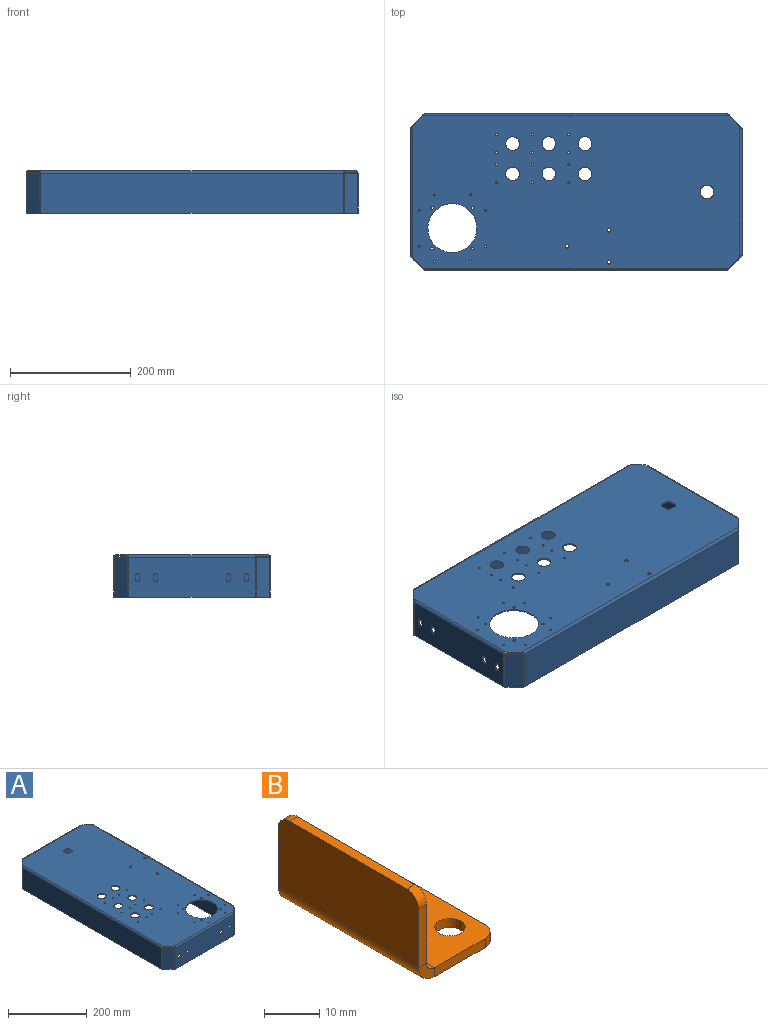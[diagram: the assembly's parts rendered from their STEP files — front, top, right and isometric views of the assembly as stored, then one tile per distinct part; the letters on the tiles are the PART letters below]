
ASSEMBLY  parts=2 mates=1
PART A: 140 faces, bbox 260x550x70 mm
  f0: plane 4.66x2mm, normal (0,-1,0), area 9.3mm2, adj f2,f3,f4,f119
  f1: plane 4.66x2mm, normal (0,1,0), area 9.3mm2, adj f3,f4,f6,f76
  f2: plane 16.83x16.83mm, normal (-0.71,-0.71,0), area 47.6mm2, adj f0,f3,f4,f127
  f3: plane 542x252mm, normal (0,0,1), area 127773.2mm2, adj f0,f1,f2,f5,f6,f7,f8,f9
  f4: plane 542x252mm, normal (0,0,-1), area 127773.2mm2, adj f0,f1,f2,f5,f6,f7,f8,f9
  f5: plane 16.83x16.83mm, normal (0.71,-0.71,0), area 47.6mm2, adj f3,f4,f15,f137
  f6: plane 16.83x16.83mm, normal (0.71,0.71,0), area 47.6mm2, adj f1,f3,f4,f136
  f7: plane 16.83x16.83mm, normal (-0.71,0.71,0), area 47.6mm2, adj f3,f4,f16,f128
  f8: cylinder r=11.25mm len=4.99mm, axis (0,0,1), area 14.4mm2, adj f3,f4,f9,f51
  f9: plane 10.11x2mm, normal (-1,0,0), area 20.2mm2, adj f3,f4,f8,f10
  f10: cylinder r=11.25mm len=4.99mm, axis (0,0,1), area 14.4mm2, adj f3,f4,f9,f11
  f11: plane 10.11x2mm, normal (0,-1,0), area 20.2mm2, adj f3,f4,f10,f12
  f12: cylinder r=11.25mm len=4.99mm, axis (0,0,1), area 14.4mm2, adj f3,f4,f11,f13
  f13: plane 10.11x2mm, normal (1,0,0), area 20.2mm2, adj f3,f4,f12,f14
  f14: cylinder r=11.25mm len=4.99mm, axis (0,0,1), area 14.4mm2, adj f3,f4,f13,f51
  f15: plane 4.66x2mm, normal (0,-1,0), area 9.3mm2, adj f3,f4,f5,f118
  f16: plane 4.66x2mm, normal (0,1,0), area 9.3mm2, adj f3,f4,f7,f75
  f17: cylinder r=11.25mm len=22.5mm, axis (0,0,1), area 141.4mm2, adj f3,f4
  f18: cylinder r=11.25mm len=22.5mm, axis (0,0,1), area 141.4mm2, adj f3,f4
  f19: cylinder r=11.25mm len=22.5mm, axis (0,0,1), area 141.4mm2, adj f3,f4
  f20: cylinder r=11.25mm len=22.5mm, axis (0,0,1), area 141.4mm2, adj f3,f4
  f21: cylinder r=11.25mm len=22.5mm, axis (0,0,1), area 141.4mm2, adj f3,f4
  f22: cylinder r=11.25mm len=22.5mm, axis (0,0,1), area 141.4mm2, adj f3,f4
  f23: cylinder r=1.75mm len=3.5mm, axis (0,0,1), area 22mm2, adj f3,f4
  f24: cylinder r=1.75mm len=3.5mm, axis (0,0,1), area 22mm2, adj f3,f4
  f25: cylinder r=1.75mm len=3.5mm, axis (0,0,1), area 22mm2, adj f3,f4
  f26: cylinder r=1.75mm len=3.5mm, axis (0,0,1), area 22mm2, adj f3,f4
  f27: cylinder r=1.75mm len=3.5mm, axis (0,0,1), area 22mm2, adj f3,f4
  f28: cylinder r=1.75mm len=3.5mm, axis (0,0,1), area 22mm2, adj f3,f4
  f29: cylinder r=1.75mm len=3.5mm, axis (0,0,1), area 22mm2, adj f3,f4
  f30: cylinder r=1.75mm len=3.5mm, axis (0,0,1), area 22mm2, adj f3,f4
  f31: cylinder r=1.75mm len=3.5mm, axis (0,0,1), area 22mm2, adj f3,f4
  f32: cylinder r=1.75mm len=3.5mm, axis (0,0,1), area 22mm2, adj f3,f4
  f33: cylinder r=1.75mm len=3.5mm, axis (0,0,1), area 22mm2, adj f3,f4
  f34: cylinder r=1.75mm len=3.5mm, axis (0,0,1), area 22mm2, adj f3,f4
  f35: cylinder r=3mm len=6mm, axis (0,0,1), area 37.7mm2, adj f3,f4
  f36: cylinder r=1.75mm len=3.5mm, axis (0,0,1), area 22mm2, adj f3,f4
  f37: cylinder r=1.75mm len=3.5mm, axis (0,0,1), area 22mm2, adj f3,f4
  f38: cylinder r=2.25mm len=4.5mm, axis (0,0,1), area 28.3mm2, adj f3,f4
  f39: cylinder r=2.25mm len=4.5mm, axis (0,0,1), area 28.3mm2, adj f3,f4
  f40: cylinder r=40.5mm len=81mm, axis (0,0,1), area 508.9mm2, adj f3,f4
  f41: cylinder r=2.25mm len=4.5mm, axis (0,0,1), area 28.3mm2, adj f3,f4
  f42: cylinder r=1.75mm len=3.5mm, axis (0,0,1), area 22mm2, adj f3,f4
  f43: cylinder r=2.25mm len=4.5mm, axis (0,0,1), area 28.3mm2, adj f3,f4
  f44: cylinder r=3mm len=6mm, axis (0,0,1), area 37.7mm2, adj f3,f4
  f45: cylinder r=3mm len=6mm, axis (0,0,1), area 37.7mm2, adj f3,f4
  f46: cylinder r=1.75mm len=3.5mm, axis (0,0,1), area 22mm2, adj f3,f4
  f47: cylinder r=1.75mm len=3.5mm, axis (0,0,1), area 22mm2, adj f3,f4
  f48: cylinder r=1.75mm len=3.5mm, axis (0,0,1), area 22mm2, adj f3,f4
  f49: cylinder r=1.75mm len=3.5mm, axis (0,0,1), area 22mm2, adj f3,f4
  f50: cylinder r=1.75mm len=3.5mm, axis (0,0,1), area 22mm2, adj f3,f4
  f51: plane 10.11x2mm, normal (0,1,0), area 20.2mm2, adj f3,f4,f8,f14
  f52: plane 209.03x2mm, normal (0,0,-1), area 418.1mm2, adj f53,f54,f62,f71
  f53: plane 209.03x66mm, normal (0,-1,0), area 13795.9mm2, adj f52,f64,f74,f78
  f54: plane 209.03x66mm, normal (0,1,0), area 13795.9mm2, adj f52,f63,f73,f77
  f55: plane 64x1.41mm, normal (0.71,-0.71,0), area 128mm2, adj f57,f58,f59,f60
  f56: plane 21.46x21.46mm, normal (0,0,1), area 56.7mm2, adj f58,f59,f60,f61
  f57: plane 22.87x22.87mm, normal (0,0,-1), area 60.7mm2, adj f55,f58,f59,f62
  f58: plane 66x21.46mm, normal (-0.71,-0.71,0), area 2001.8mm2, adj f55,f56,f57,f60,f64
  f59: plane 66x21.46mm, normal (0.71,0.71,0), area 2001.8mm2, adj f55,f56,f57,f60,f63
  f60: cylinder r=2mm len=2.83mm, axis (-0.71,-0.71,0), area 6.3mm2, adj f55,f56,f58,f59
  f61: plane 2.83x2.59mm, normal (0,0,1), area 4.7mm2, adj f56,f63,f64,f76
  f62: plane 2.83x2.59mm, normal (0,0,-1), area 4.7mm2, adj f52,f57,f63,f64
  f63: cylinder r=4mm len=66mm, axis (0,0,1), area 207.3mm2, adj f54,f59,f61,f62
  f64: cylinder r=2mm len=66mm, axis (0,0,1), area 103.7mm2, adj f53,f58,f61,f62
  f65: plane 64x1.41mm, normal (-0.71,-0.71,0), area 128mm2, adj f66,f68,f69,f70
  f66: plane 22.87x22.87mm, normal (0,0,-1), area 60.7mm2, adj f65,f68,f69,f71
  f67: plane 21.46x21.46mm, normal (0,0,1), area 56.7mm2, adj f68,f69,f70,f72
  f68: plane 66x21.46mm, normal (0.71,-0.71,0), area 2001.8mm2, adj f65,f66,f67,f70,f74
  f69: plane 66x21.46mm, normal (-0.71,0.71,0), area 2001.8mm2, adj f65,f66,f67,f70,f73
  f70: cylinder r=2mm len=2.83mm, axis (0.71,-0.71,0), area 6.3mm2, adj f65,f67,f68,f69
  f71: plane 2.83x2.59mm, normal (0,0,-1), area 4.7mm2, adj f52,f66,f73,f74
  f72: plane 2.83x2.59mm, normal (0,0,1), area 4.7mm2, adj f67,f73,f74,f75
  f73: cylinder r=4mm len=66mm, axis (0,0,-1), area 207.3mm2, adj f54,f69,f71,f72
  f74: cylinder r=2mm len=66mm, axis (0,0,-1), area 103.7mm2, adj f53,f68,f71,f72
  f75: plane 4x4mm, normal (-1,0,0), area 9.4mm2, adj f16,f72,f77,f78
  f76: plane 4x4mm, normal (1,0,0), area 9.4mm2, adj f1,f61,f77,f78
  f77: cylinder r=4mm len=209.03mm, axis (-1,0,0), area 1313.4mm2, adj f3,f54,f75,f76
  f78: cylinder r=2mm len=209.03mm, axis (-1,0,0), area 656.7mm2, adj f4,f53,f75,f76
  f79: plane 6x2mm, normal (-1,0,0), area 12mm2, adj f80,f95,f96,f97
  f80: cylinder r=3.5mm len=7mm, axis (0,1,0), area 22mm2, adj f79,f81,f96,f97
  f81: plane 6x2mm, normal (1,0,0), area 12mm2, adj f80,f95,f96,f97
  f82: plane 6x2mm, normal (-1,0,0), area 12mm2, adj f83,f94,f96,f97
  f83: cylinder r=3.5mm len=7mm, axis (0,1,0), area 22mm2, adj f82,f84,f96,f97
  f84: plane 6x2mm, normal (1,0,0), area 12mm2, adj f83,f94,f96,f97
  f85: plane 6x2mm, normal (1,0,0), area 12mm2, adj f86,f93,f96,f97
  f86: cylinder r=3.5mm len=7mm, axis (0,1,0), area 22mm2, adj f85,f87,f96,f97
  f87: plane 6x2mm, normal (-1,0,0), area 12mm2, adj f86,f93,f96,f97
  f88: plane 6x2mm, normal (1,0,0), area 12mm2, adj f89,f92,f96,f97
  f89: cylinder r=3.5mm len=7mm, axis (0,1,0), area 22mm2, adj f88,f90,f96,f97
  f90: plane 6x2mm, normal (-1,0,0), area 12mm2, adj f89,f92,f96,f97
  f91: plane 209.03x2mm, normal (0,0,-1), area 418.1mm2, adj f96,f97,f105,f114
  f92: cylinder r=3.5mm len=7mm, axis (0,1,0), area 22mm2, adj f88,f90,f96,f97
  f93: cylinder r=3.5mm len=7mm, axis (0,1,0), area 22mm2, adj f85,f87,f96,f97
  f94: cylinder r=3.5mm len=7mm, axis (0,1,0), area 22mm2, adj f82,f84,f96,f97
  f95: cylinder r=3.5mm len=7mm, axis (0,1,0), area 22mm2, adj f79,f81,f96,f97
  f96: plane 209.03x66mm, normal (0,1,0), area 13474mm2, adj f79,f80,f81,f82,f83,f84,f85,f86
  f97: plane 209.03x66mm, normal (0,-1,0), area 13474mm2, adj f79,f80,f81,f82,f83,f84,f85,f86
  f98: plane 64x1.41mm, normal (-0.71,0.71,0), area 128mm2, adj f100,f101,f102,f103
  f99: plane 21.46x21.46mm, normal (0,0,1), area 56.7mm2, adj f101,f102,f103,f104
  f100: plane 22.87x22.87mm, normal (0,0,-1), area 60.7mm2, adj f98,f101,f102,f105
  f101: plane 66x21.46mm, normal (0.71,0.71,0), area 2001.8mm2, adj f98,f99,f100,f103,f107
  f102: plane 66x21.46mm, normal (-0.71,-0.71,0), area 2001.8mm2, adj f98,f99,f100,f103,f106
  f103: cylinder r=2mm len=2.83mm, axis (0.71,0.71,0), area 6.3mm2, adj f98,f99,f101,f102
  f104: plane 2.83x2.59mm, normal (0,0,1), area 4.7mm2, adj f99,f106,f107,f119
  f105: plane 2.83x2.59mm, normal (0,0,-1), area 4.7mm2, adj f91,f100,f106,f107
  f106: cylinder r=4mm len=66mm, axis (0,0,1), area 207.3mm2, adj f97,f102,f104,f105
  f107: cylinder r=2mm len=66mm, axis (0,0,1), area 103.7mm2, adj f96,f101,f104,f105
  f108: plane 64x1.41mm, normal (0.71,0.71,0), area 128mm2, adj f109,f111,f112,f113
  f109: plane 22.87x22.87mm, normal (0,0,-1), area 60.7mm2, adj f108,f111,f112,f114
  f110: plane 21.46x21.46mm, normal (0,0,1), area 56.7mm2, adj f111,f112,f113,f115
  f111: plane 66x21.46mm, normal (-0.71,0.71,0), area 2001.8mm2, adj f108,f109,f110,f113,f117
  f112: plane 66x21.46mm, normal (0.71,-0.71,0), area 2001.8mm2, adj f108,f109,f110,f113,f116
  f113: cylinder r=2mm len=2.83mm, axis (-0.71,0.71,0), area 6.3mm2, adj f108,f110,f111,f112
  f114: plane 2.83x2.59mm, normal (0,0,-1), area 4.7mm2, adj f91,f109,f116,f117
  f115: plane 2.83x2.59mm, normal (0,0,1), area 4.7mm2, adj f110,f116,f117,f118
  f116: cylinder r=4mm len=66mm, axis (0,0,-1), area 207.3mm2, adj f97,f112,f114,f115
  f117: cylinder r=2mm len=66mm, axis (0,0,-1), area 103.7mm2, adj f96,f111,f114,f115
  f118: plane 4x4mm, normal (1,0,0), area 9.4mm2, adj f15,f115,f120,f121
  f119: plane 4x4mm, normal (-1,0,0), area 9.4mm2, adj f0,f104,f120,f121
  f120: cylinder r=4mm len=209.03mm, axis (1,0,0), area 1313.4mm2, adj f3,f97,f118,f119
  f121: cylinder r=2mm len=209.03mm, axis (1,0,0), area 656.7mm2, adj f4,f96,f118,f119
  f122: plane 500.34x2mm, normal (0,0,-1), area 1000.7mm2, adj f123,f124,f125,f126
  f123: plane 66x2mm, normal (0,1,0), area 132mm2, adj f122,f125,f126,f128
  f124: plane 66x2mm, normal (0,-1,0), area 132mm2, adj f122,f125,f126,f127
  f125: plane 500.34x66mm, normal (1,0,0), area 33022.6mm2, adj f122,f123,f124,f130
  f126: plane 500.34x66mm, normal (-1,0,0), area 33022.6mm2, adj f122,f123,f124,f129
  f127: bspline ~4x4mm, area 12.8mm2, adj f2,f124,f129,f130
  f128: bspline ~4x4mm, area 12.8mm2, adj f7,f123,f129,f130
  f129: cylinder r=4mm len=508.34mm, axis (0,-1,0), area 3162mm2, adj f3,f126,f127,f128
  f130: cylinder r=2mm len=508.34mm, axis (0,-1,0), area 1581mm2, adj f4,f125,f127,f128
  f131: plane 500.34x2mm, normal (0,0,-1), area 1000.7mm2, adj f132,f133,f134,f135
  f132: plane 66x2mm, normal (0,-1,0), area 132mm2, adj f131,f134,f135,f137
  f133: plane 66x2mm, normal (0,1,0), area 132mm2, adj f131,f134,f135,f136
  f134: plane 500.34x66mm, normal (-1,0,0), area 33022.6mm2, adj f131,f132,f133,f139
  f135: plane 500.34x66mm, normal (1,0,0), area 33022.6mm2, adj f131,f132,f133,f138
  f136: bspline ~4x4mm, area 12.8mm2, adj f6,f133,f138,f139
  f137: bspline ~4x4mm, area 12.8mm2, adj f5,f132,f138,f139
  f138: cylinder r=4mm len=508.34mm, axis (0,1,0), area 3162mm2, adj f3,f135,f136,f137
  f139: cylinder r=2mm len=508.34mm, axis (0,1,0), area 1581mm2, adj f4,f134,f136,f137
PART B: 20 faces, bbox 20x36x20 mm
  f0: plane 13x2mm, normal (0,-1,0), area 26mm2, adj f1,f5,f6,f7
  f1: cylinder r=3mm len=3mm, axis (-1,0,0), area 9.4mm2, adj f0,f2,f5,f7
  f2: plane 30x2mm, normal (0,0,1), area 60mm2, adj f1,f3,f5,f7
  f3: cylinder r=3mm len=3mm, axis (-1,0,0), area 9.4mm2, adj f2,f4,f5,f7
  f4: plane 13x2mm, normal (0,1,0), area 26mm2, adj f3,f5,f7,f8
  f5: plane 36x16mm, normal (1,0,0), area 572.1mm2, adj f0,f1,f2,f3,f4,f9
  f6: plane 4x4mm, normal (0,-1,0), area 9.4mm2, adj f0,f9,f10,f11
  f7: plane 36x16mm, normal (-1,0,0), area 572.1mm2, adj f0,f1,f2,f3,f4,f11
  f8: plane 4x4mm, normal (0,1,0), area 9.4mm2, adj f4,f9,f11,f12
  f9: cylinder r=2mm len=36mm, axis (0,-1,0), area 113.1mm2, adj f5,f6,f8,f17
  f10: plane 13x2mm, normal (0,-1,0), area 26mm2, adj f6,f15,f17,f18
  f11: cylinder r=4mm len=36mm, axis (0,-1,0), area 226.2mm2, adj f6,f7,f8,f18
  f12: plane 13x2mm, normal (0,1,0), area 26mm2, adj f8,f13,f17,f18
  f13: cylinder r=3mm len=3mm, axis (0,0,1), area 9.4mm2, adj f12,f14,f17,f18
  f14: plane 30x2mm, normal (1,0,0), area 60mm2, adj f13,f15,f17,f18
  f15: cylinder r=3mm len=3mm, axis (0,0,1), area 9.4mm2, adj f10,f14,f17,f18
  f16: cylinder r=2.75mm len=5.5mm, axis (0,0,-1), area 34.6mm2, adj f17,f18
  f17: plane 36x16mm, normal (0,0,1), area 524.6mm2, adj f9,f10,f12,f13,f14,f15,f16,f19
  f18: plane 36x16mm, normal (0,0,-1), area 524.6mm2, adj f10,f11,f12,f13,f14,f15,f16,f19
  f19: cylinder r=2.75mm len=5.5mm, axis (0,0,-1), area 34.6mm2, adj f17,f18
PLACE A rot(axis=(0,0,-1),90deg) t=(-516.82,65.92,34.12)mm
PLACE B rot(axis=(0,0,-1),90deg) t=(-262.2,60.92,-33.83)mm
MATE fastened B.f7 <-> A.f125  axis (0,1,0) through (-667.2,188.92,-8.88)mm
